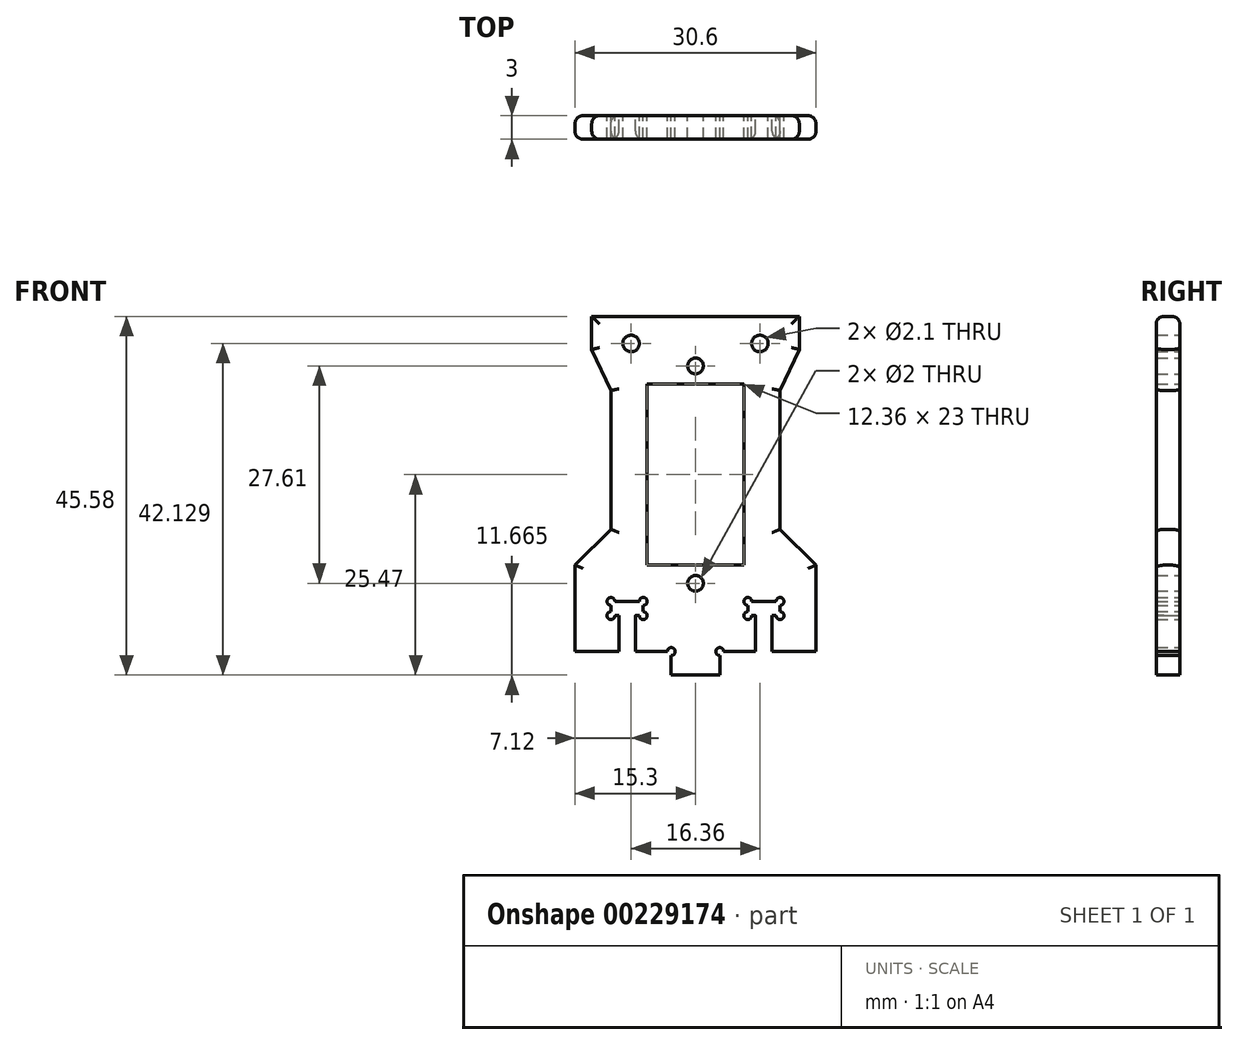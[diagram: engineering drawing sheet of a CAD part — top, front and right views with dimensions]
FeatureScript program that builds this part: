
annotation { "Feature Type Name" : "Feature", "Feature Type Description" : "" }
export const myFeature = defineFeature(function(context is Context, id is Id, definition is map)
    precondition{}
    {
        {
            var Q0;
            Q0=qCreatedBy(makeId("Front.planeOp"),FACE);
            var sketch = newSketch(context, id + "F0", { "sketchPlane" : qUnion([Q0])});
            skLineSegment(sketch, "E0.bottom", {"start": v(10.24, -16.1) * mm, "end": v(7.14, -16.1) * mm});
            skLineSegment(sketch, "E0.left", {"start": v(10.74, -16.1) * mm, "end": v(10.74, 10.68) * mm});
            skLineSegment(sketch, "E0.right", {"start": v(-10.74, -15.6) * mm, "end": v(-10.74, 10.68) * mm});
            skPoint(sketch, "E0.middle", {"position": v(0, 0) * mm});
            skLineSegment(sketch, "E1.bottom", {"start": v(6.18, -11.5) * mm, "end": v(-6.18, -11.5) * mm});
            skLineSegment(sketch, "E1.top", {"start": v(6.18, 11.5) * mm, "end": v(-6.18, 11.5) * mm});
            skLineSegment(sketch, "E1.left", {"start": v(6.18, -11.5) * mm, "end": v(6.18, 11.5) * mm});
            skLineSegment(sketch, "E1.right", {"start": v(-6.18, -11.5) * mm, "end": v(-6.18, 11.5) * mm});
            skCircle(sketch, "E2", {"center": v(0, 13.8) * mm, "radius": 1 * mm});
            skCircle(sketch, "E3", {"center": v(0, -13.8) * mm, "radius": 1 * mm});
            skLineSegment(sketch, "E4", {"start": v(-6.18, -11.5) * mm, "end": v(-6.18, -16.1) * mm});
            skLineSegment(sketch, "E5", {"start": v(6.18, -11.5) * mm, "end": v(6.18, -16.1) * mm});
            skLineSegment(sketch, "E6.bottom", {"start": v(-10.24, -16.1) * mm, "end": v(-7.14, -16.1) * mm});
            skLineSegment(sketch, "E6.top", {"start": v(-10.24, -17.9) * mm, "end": v(-9.74, -17.9) * mm});
            skLineSegment(sketch, "E6.left", {"start": v(-10.74, -16.6) * mm, "end": v(-10.74, -17.4) * mm});
            skLineSegment(sketch, "E6.right", {"start": v(-6.64, -16.6) * mm, "end": v(-6.64, -17.4) * mm});
            skLineSegment(sketch, "E7.top", {"start": v(10.24, -17.9) * mm, "end": v(9.74, -17.9) * mm});
            skLineSegment(sketch, "E7.left", {"start": v(10.74, -16.6) * mm, "end": v(10.74, -17.4) * mm});
            skLineSegment(sketch, "E7.right", {"start": v(6.64, -16.6) * mm, "end": v(6.64, -17.4) * mm});
            skLineSegment(sketch, "E8.bottom", {"start": v(-15.3, -11.5) * mm, "end": v(15.3, -11.5) * mm});
            skLineSegment(sketch, "E8.top", {"start": v(-15.3, -22.47) * mm, "end": v(-9.74, -22.47) * mm});
            skLineSegment(sketch, "E8.left", {"start": v(-15.3, -11.5) * mm, "end": v(-15.3, -22.47) * mm});
            skLineSegment(sketch, "E8.right", {"start": v(15.3, -11.5) * mm, "end": v(15.3, -22.47) * mm});
            skLineSegment(sketch, "E9", {"start": v(-15.3, -11.5) * mm, "end": v(-10.74, -6.94) * mm});
            skLineSegment(sketch, "E10", {"start": v(15.3, -11.5) * mm, "end": v(10.74, -6.94) * mm});
            skLineSegment(sketch, "E11.left", {"start": v(-9.74, -17.91) * mm, "end": v(-9.74, -22.47) * mm});
            skLineSegment(sketch, "E11.right", {"start": v(-7.64, -17.91) * mm, "end": v(-7.64, -22.47) * mm});
            skLineSegment(sketch, "E12.left", {"start": v(7.64, -17.9) * mm, "end": v(7.64, -22.47) * mm});
            skLineSegment(sketch, "E12.right", {"start": v(9.74, -17.9) * mm, "end": v(9.74, -22.47) * mm});
            skPoint(sketch, "E13", {"position": v(-8.7, -17.9) * mm});
            skPoint(sketch, "E14", {"position": v(8.7, -17.9) * mm});
            skLineSegment(sketch, "E15.bottom", {"start": v(-2.58, -22.47) * mm, "end": v(2.58, -22.47) * mm});
            skLineSegment(sketch, "E15.top", {"start": v(-3.08, -25.47) * mm, "end": v(3.08, -25.47) * mm});
            skLineSegment(sketch, "E15.left", {"start": v(-3.08, -22.97) * mm, "end": v(-3.08, -25.47) * mm});
            skLineSegment(sketch, "E15.right", {"start": v(3.08, -22.97) * mm, "end": v(3.08, -25.47) * mm});
            skPoint(sketch, "E16", {"position": v(0, -22.47) * mm});
            skArc(sketch, "E17", {"start": v(-10.74, -17.4) * mm, "mid": v(-11.1, -18.26) * mm, "end": v(-10.24, -17.9) * mm});
            skArc(sketch, "E18", {"start": v(-10.24, -16.1) * mm, "mid": v(-11.1, -15.76) * mm, "end": v(-10.74, -16.6) * mm});
            skArc(sketch, "E19", {"start": v(-6.64, -16.6) * mm, "mid": v(-6.29, -15.76) * mm, "end": v(-7.14, -16.1) * mm});
            skArc(sketch, "E20", {"start": v(-7.14, -17.9) * mm, "mid": v(-6.29, -18.26) * mm, "end": v(-6.64, -17.4) * mm});
            skArc(sketch, "E21", {"start": v(7.14, -16.1) * mm, "mid": v(6.29, -15.76) * mm, "end": v(6.64, -16.6) * mm});
            skArc(sketch, "E22", {"start": v(6.64, -17.4) * mm, "mid": v(6.29, -18.26) * mm, "end": v(7.14, -17.9) * mm});
            skArc(sketch, "E23", {"start": v(10.74, -16.6) * mm, "mid": v(11.1, -15.76) * mm, "end": v(10.24, -16.1) * mm});
            skArc(sketch, "E24", {"start": v(10.24, -17.9) * mm, "mid": v(11.1, -18.26) * mm, "end": v(10.74, -17.4) * mm});
            skArc(sketch, "E25", {"start": v(3.58, -22.47) * mm, "mid": v(2.73, -22.12) * mm, "end": v(3.08, -22.97) * mm});
            skArc(sketch, "E26", {"start": v(-3.08, -22.97) * mm, "mid": v(-2.73, -22.12) * mm, "end": v(-3.58, -22.47) * mm});
            skLineSegment(sketch, "E27.trimOffspring", {"start": v(-7.14, -16.1) * mm, "end": v(-10.24, -16.1) * mm});
            skLineSegment(sketch, "E28.trimOffspring", {"start": v(3.58, -22.47) * mm, "end": v(7.64, -22.47) * mm});
            skLineSegment(sketch, "E29.trimOffspring", {"start": v(7.64, -17.9) * mm, "end": v(7.14, -17.9) * mm});
            skLineSegment(sketch, "E30.trimOffspring", {"start": v(6.18, -16.1) * mm, "end": v(-6.18, -16.1) * mm});
            skLineSegment(sketch, "E31.trimOffspring", {"start": v(9.74, -22.47) * mm, "end": v(15.3, -22.47) * mm});
            skLineSegment(sketch, "E32.trimOffspring", {"start": v(-7.64, -17.9) * mm, "end": v(-7.14, -17.9) * mm});
            skLineSegment(sketch, "E33.trimOffspring", {"start": v(-7.64, -22.47) * mm, "end": v(-3.58, -22.47) * mm});
            skCircle(sketch, "E34", {"center": v(-8.18, 16.66) * mm, "radius": 1.05 * mm});
            skCircle(sketch, "E35", {"center": v(8.18, 16.66) * mm, "radius": 1.05 * mm});
            skLineSegment(sketch, "E36", {"start": v(10.74, 10.68) * mm, "end": v(13.18, 15.9) * mm});
            skLineSegment(sketch, "E37", {"start": v(-10.74, 10.68) * mm, "end": v(-13.18, 15.9) * mm});
            skLineSegment(sketch, "E38", {"start": v(-13.18, 15.9) * mm, "end": v(-13.18, 20.1) * mm});
            skLineSegment(sketch, "E39", {"start": v(-13.18, 20.1) * mm, "end": v(13.18, 20.1) * mm});
            skLineSegment(sketch, "E40", {"start": v(13.18, 20.1) * mm, "end": v(13.18, 15.9) * mm});
            skCircle(sketch, "E41", {"center": v(0, 5.32) * mm, "radius": 6.18 * mm, "construction": true});
            skPoint(sketch, "E41.centerSnap0", {"position": v(0, 11.5) * mm});
            skLineSegment(sketch, "E42", {"start": v(-6.18, -16.1) * mm, "end": v(6.18, -11.5) * mm, "construction": true});
            skLineSegment(sketch, "E43", {"start": v(6.18, -16.1) * mm, "end": v(-6.18, -11.5) * mm, "construction": true});
            skLineSegment(sketch, "E44.bottom", {"start": v(6.18, 11.5) * mm, "end": v(-6.18, 11.5) * mm, "construction": true});
            skLineSegment(sketch, "E44.top", {"start": v(6.18, 16.1) * mm, "end": v(-6.18, 16.1) * mm, "construction": true});
            skLineSegment(sketch, "E44.left", {"start": v(6.18, 11.5) * mm, "end": v(6.18, 16.1) * mm, "construction": true});
            skLineSegment(sketch, "E44.right", {"start": v(-6.18, 11.5) * mm, "end": v(-6.18, 16.1) * mm, "construction": true});
            skLineSegment(sketch, "E45", {"start": v(-6.18, 11.5) * mm, "end": v(6.18, 16.1) * mm, "construction": true});
            skLineSegment(sketch, "E46", {"start": v(6.18, 11.5) * mm, "end": v(-6.18, 16.1) * mm, "construction": true});
            skSolve(sketch);
        }
        {
            var Q0;
            Q0=makeQuery(id+"F0.imprint","IMPRINT",FACE,{"disambiguationData":[TD([[makeQuery(id+"F0.imprint","IMPRINT",EDGE,{"derivedFrom":sQuery(id+"F0.wireOp",EDGE,"E15.bottom")}),-1.0]])]});
            var Q1;
            {var subQ0=sQuery(id+"F0.wireOp",EDGE,"E10");Q1=makeQuery(id+"F0.imprint","IMPRINT",FACE,{"disambiguationData":[TD([[makeQuery(id+"F0.imprint","IMPRINT",EDGE,{"derivedFrom":subQ0}),1.0]])]});}
            var Q2;
            {var subQ0=sQuery(id+"F0.wireOp",EDGE,"E9");Q2=makeQuery(id+"F0.imprint","IMPRINT",FACE,{"disambiguationData":[TD([[makeQuery(id+"F0.imprint","IMPRINT",EDGE,{"derivedFrom":subQ0}),-1.0]])]});}
            var Q3;
            Q3=makeQuery(id+"F0.imprint","IMPRINT",FACE,{"disambiguationData":[TD([[makeQuery(id+"F0.imprint","IMPRINT",EDGE,{"derivedFrom":sQuery(id+"F0.wireOp",EDGE,"ZplLBCht-MEbq-9qZc-Yp2g-QLO0PEXXqDaA.top")}),-1.0]])]});
            var Q4;
            Q4=makeQuery(id+"F0.imprint","IMPRINT",FACE,{"disambiguationData":[TD([[makeQuery(id+"F0.imprint","IMPRINT",EDGE,{"derivedFrom":sQuery(id+"F0.wireOp",EDGE,"E7.top")}),1.0]])]});
            var Q5;
            Q5=makeQuery(id+"F0.imprint","IMPRINT",FACE,{"disambiguationData":[TD([[makeQuery(id+"F0.imprint","IMPRINT",EDGE,{"derivedFrom":sQuery(id+"F0.wireOp",EDGE,"E6.top")}),-1.0]])]});
            var Q6;
            Q6=makeQuery(id+"F0.imprint","IMPRINT",FACE,{"disambiguationData":[TD([[makeQuery(id+"F0.imprint","IMPRINT",EDGE,{"derivedFrom":sQuery(id+"F0.wireOp",EDGE,"E1.top")}),-1.0]])]});
            var Q7;
            Q7=makeQuery(id+"F0.imprint","IMPRINT",FACE,{"disambiguationData":[TD([[makeQuery(id+"F0.imprint","IMPRINT",EDGE,{"derivedFrom":sQuery(id+"F0.wireOp",EDGE,"E1.top")}),-1.0]])]});
            var Q8;
            {var subQ8=sQuery(id+"F0.wireOp",EDGE,"E6.right");Q8=makeQuery(id+"F0.imprint","IMPRINT",FACE,{"disambiguationData":[TD([[makeQuery(id+"F0.imprint","IMPRINT",EDGE,{"derivedFrom":subQ8}),1.0]])]});}
            var Q9;
            Q9=makeQuery(id+"F0.imprint","IMPRINT",FACE,{"disambiguationData":[TD([[makeQuery(id+"F0.imprint","IMPRINT",EDGE,{"derivedFrom":sQuery(id+"F0.wireOp",EDGE,"E1.top")}),-1.0]])]});
            var Q10;
            {var subQ2=sQuery(id+"F0.wireOp",EDGE,"E1.bottom");Q10=makeQuery(id+"F0.imprint","IMPRINT",FACE,{"disambiguationData":[TD([[makeQuery(id+"F0.imprint","IMPRINT",EDGE,{"derivedFrom":subQ2}),1.0]])]});}
            var Q11;
            {var subQ0=sQuery(id+"F0.wireOp",EDGE,"E6.bottom");Q11=makeQuery(id+"F0.imprint","IMPRINT",FACE,{"disambiguationData":[TD([[makeQuery(id+"F0.imprint","IMPRINT",EDGE,{"derivedFrom":subQ0}),1.0]])]});}
            var Q12;
            {var subQ9=sQuery(id+"F0.wireOp",EDGE,"E0.bottom");Q12=makeQuery(id+"F0.imprint","IMPRINT",FACE,{"disambiguationData":[TD([[makeQuery(id+"F0.imprint","IMPRINT",EDGE,{"derivedFrom":subQ9}),-1.0]])]});}
            var Q13;
            {var subQ2=sQuery(id+"F0.wireOp",EDGE,"E15.bottom");Q13=makeQuery(id+"F0.imprint","IMPRINT",FACE,{"disambiguationData":[TD([[makeQuery(id+"F0.imprint","IMPRINT",EDGE,{"derivedFrom":subQ2}),-1.0]])]});}
            extrude(context, id + "F1", {"entities" : qUnion([Q0, Q1, Q2, Q3, Q4, Q5, Q6, Q7, Q8, Q9, Q10, Q11, Q12, Q13]), "depth" : 3 * mm});
        }
        {
            var Q0;
            Q0=makeQuery(id+"F1.opExtrude","CAP_EDGE",EDGE,{"disambiguationData":[OSD([sQuery(id+"F0.wireOp",EDGE,"E39")])],"isStart":false});
            var Q1;
            Q1=makeQuery(id+"F1.opExtrude","CAP_EDGE",EDGE,{"disambiguationData":[OSD([sQuery(id+"F0.wireOp",EDGE,"E38")])],"isStart":false});
            var Q2;
            Q2=makeQuery(id+"F1.opExtrude","CAP_EDGE",EDGE,{"disambiguationData":[OSD([sQuery(id+"F0.wireOp",EDGE,"E37")])],"isStart":false});
            var Q3;
            Q3=makeQuery(id+"F1.opExtrude","CAP_EDGE",EDGE,{"disambiguationData":[OSD([sQuery(id+"F0.wireOp",EDGE,"E0.right")])],"isStart":false});
            var Q4;
            Q4=makeQuery(id+"F1.opExtrude","CAP_EDGE",EDGE,{"disambiguationData":[OSD([sQuery(id+"F0.wireOp",EDGE,"E9")])],"isStart":false});
            var Q5;
            Q5=makeQuery(id+"F1.opExtrude","CAP_EDGE",EDGE,{"disambiguationData":[OSD([sQuery(id+"F0.wireOp",EDGE,"E8.left")])],"isStart":false});
            var Q6;
            Q6=makeQuery(id+"F1.opExtrude","CAP_EDGE",EDGE,{"disambiguationData":[OSD([sQuery(id+"F0.wireOp",EDGE,"E8.right")])],"isStart":false});
            var Q7;
            Q7=makeQuery(id+"F1.opExtrude","CAP_EDGE",EDGE,{"disambiguationData":[OSD([sQuery(id+"F0.wireOp",EDGE,"E10")])],"isStart":false});
            var Q8;
            Q8=makeQuery(id+"F1.opExtrude","CAP_EDGE",EDGE,{"disambiguationData":[OSD([sQuery(id+"F0.wireOp",EDGE,"E0.left")])],"isStart":false});
            var Q9;
            Q9=makeQuery(id+"F1.opExtrude","CAP_EDGE",EDGE,{"disambiguationData":[OSD([sQuery(id+"F0.wireOp",EDGE,"E36")])],"isStart":false});
            var Q10;
            Q10=makeQuery(id+"F1.opExtrude","CAP_EDGE",EDGE,{"disambiguationData":[OSD([sQuery(id+"F0.wireOp",EDGE,"E40")])],"isStart":false});
            var Q11;
            Q11=makeQuery(id+"F1.opExtrude","CAP_EDGE",EDGE,{"disambiguationData":[OSD([sQuery(id+"F0.wireOp",EDGE,"E12.left")])],"isStart":false});
            var Q12;
            Q12=makeQuery(id+"F1.opExtrude","CAP_EDGE",EDGE,{"disambiguationData":[OSD([sQuery(id+"F0.wireOp",EDGE,"E12.right")])],"isStart":false});
            var Q13;
            Q13=makeQuery(id+"F1.opExtrude","CAP_EDGE",EDGE,{"disambiguationData":[OSD([sQuery(id+"F0.wireOp",EDGE,"E11.right")])],"isStart":false});
            var Q14;
            Q14=makeQuery(id+"F1.opExtrude","CAP_EDGE",EDGE,{"disambiguationData":[OSD([sQuery(id+"F0.wireOp",EDGE,"E11.left")])],"isStart":false});
            var Q15;
            Q15=makeQuery(id+"F1.opExtrude","CAP_EDGE",EDGE,{"disambiguationData":[OSD([sQuery(id+"F0.wireOp",EDGE,"E39")])],"isStart":true});
            var Q16;
            Q16=makeQuery(id+"F1.opExtrude","CAP_EDGE",EDGE,{"disambiguationData":[OSD([sQuery(id+"F0.wireOp",EDGE,"E40")])],"isStart":true});
            var Q17;
            Q17=makeQuery(id+"F1.opExtrude","CAP_EDGE",EDGE,{"disambiguationData":[OSD([sQuery(id+"F0.wireOp",EDGE,"E36")])],"isStart":true});
            var Q18;
            Q18=makeQuery(id+"F1.opExtrude","CAP_EDGE",EDGE,{"disambiguationData":[OSD([sQuery(id+"F0.wireOp",EDGE,"E38")])],"isStart":true});
            var Q19;
            Q19=makeQuery(id+"F1.opExtrude","CAP_EDGE",EDGE,{"disambiguationData":[OSD([sQuery(id+"F0.wireOp",EDGE,"E37")])],"isStart":true});
            var Q20;
            Q20=makeQuery(id+"F1.opExtrude","CAP_EDGE",EDGE,{"disambiguationData":[OSD([sQuery(id+"F0.wireOp",EDGE,"E0.right")])],"isStart":true});
            var Q21;
            Q21=makeQuery(id+"F1.opExtrude","CAP_EDGE",EDGE,{"disambiguationData":[OSD([sQuery(id+"F0.wireOp",EDGE,"E9")])],"isStart":true});
            var Q22;
            Q22=makeQuery(id+"F1.opExtrude","CAP_EDGE",EDGE,{"disambiguationData":[OSD([sQuery(id+"F0.wireOp",EDGE,"E8.left")])],"isStart":true});
            var Q23;
            Q23=makeQuery(id+"F1.opExtrude","CAP_EDGE",EDGE,{"disambiguationData":[OSD([sQuery(id+"F0.wireOp",EDGE,"E8.right")])],"isStart":true});
            var Q24;
            Q24=makeQuery(id+"F1.opExtrude","CAP_EDGE",EDGE,{"disambiguationData":[OSD([sQuery(id+"F0.wireOp",EDGE,"E10")])],"isStart":true});
            var Q25;
            Q25=makeQuery(id+"F1.opExtrude","CAP_EDGE",EDGE,{"disambiguationData":[OSD([sQuery(id+"F0.wireOp",EDGE,"E0.left")])],"isStart":true});
            fillet(context, id + "F2", {"entities" : qUnion([Q0, Q1, Q2, Q3, Q4, Q5, Q6, Q7, Q8, Q9, Q10, Q11, Q12, Q13, Q14, Q15, Q16, Q17, Q18, Q19, Q20, Q21, Q22, Q23, Q24, Q25]), "radius" : 1 * mm, "tangentPropagation" : true, "allowEdgeOverflow" : false});
        }
    });
